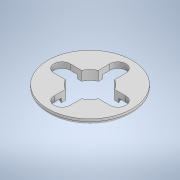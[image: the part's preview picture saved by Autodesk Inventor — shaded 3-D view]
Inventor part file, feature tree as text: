
AUTODESK INVENTOR PART (.ipt)
format: ipt  version: 2021 (Build 250183000, 183)  size: 172,544 bytes
history: native  units: mm
features: extrude x4, sketch x3, fillet x1
ambient origin geometry x8: Origin, YZ Plane, XZ Plane, XY Plane, X Axis, Y Axis, Z Axis, Center Point
bodies: Solid1 (feature_tree)
feature tree (8):
  sketch  "Sketch1"  dims[d2=45.5mm d4=55.0mm]
  extrude  "Extrusion1"  Depth=55.0mm
  extrude  "Extrusion2"  Depth=7.0mm TaperAngle=0.0deg
  fillet  "Fillet1"  Radius=4.0mm
  sketch  "Sketch2"  dims[d5=4.75mm d6=0.0mm d7=7.0mm d8=0.0mm d9=4.0mm]
  extrude  "Extrusion3"  TaperAngle=0.0deg  [1 undecoded]
  extrude  "Extrusion5"  Depth=40.0mm TaperAngle=360.0deg
  sketch  "Sketch3"  dims[d12=40.0mm d14=360.0deg d16=0.0mm d17=0.0mm d20=40.0mm d22=360.0deg d24=0.0mm d25=0.0mm]
note: 1 required parameter value undecoded (feature->parameter linkage not recoverable at this tier; creation-order binding heuristic only, values carry confidence <= 0.55)
